# Revit family: Ytong prefabrikované betonové překlady
name_source: partatom
category: Konstrukční rámová konstrukce
units: mm (PartAtom-declared; Revit-internal decimal feet)

## family parameters
Materiál pro modelové chování = Jiné
Ořezat dutým tvarem při načtení = Ne
Sdílené = Ano
Tvar řezu = Není definováno
Vždy exportovat jako geometrii = Ne
Vždy vertikální = Ano
Založené na pracovní rovině = Ne
Zaokrouhlení délky rámové konstrukce = 0 mm
Zobrazit v půdorysech řeznou rovinu rodiny = Ano

## types (1)
- Ytong prefabrikované betonové překlady
    Autor = BIM Technology s.r.o.
    Faktor difúzního odporu μ (EN 1745) = 29
    Hláška při nenalezení = Překročena maximální světlost otvoru!
    IfcExportAs = IfcBeam
    IfcExportType = LINTEL
    Krátký popis = Betonové prvky vyztužené betonářskou výztuží.
    Materiál = beton C 25/30
    Max. průměrná objemová hmotnost v suchém stavu (EN 772-13) [kg/m3] = 2450
    Minimální délka nosníku = 1000 mm  [stored 3.28084 ft]
    Název tabulky = Ytong prefabrikované betonové překlady
    Odkaz na stavební postup = https://storefrontapi.commerce.xella.com
    Odkaz na technický list = https://storefrontapi.commerce.xella.com
    Odkaz na web = https://www.xella.cz
    Popis = Betonové prvky vyztužené betonářskou výztuží.
    Požární odolnost = R 30
    Skupina prvků = Překlad
    Součinitel tep. vodivosti lambda = 1.5800 W/(m·K)
    Trvanlivost (proti korozi) = D1
    URL = https://www.xella.cz
    Výrobce = Ytong
    Zobrazit ve výkazech = Ano

note: [stored X ft] marks values corroborated as IEEE doubles in the binary element streams (Revit-internal decimal feet)
